# Revit family: Plymold-Essentials-Round_Pedestal-
name_source: partatom
category: Furniture
units: mm (PartAtom-declared; Revit-internal decimal feet)

## family parameters
Always vertical = Yes
Cut with Voids When Loaded = No
OmniClass Number = 23.40.20.00
OmniClass Title = General Furniture and Specialties
Render Appearance Source = Family Geometry
Room Calculation Point = No
Shared = No
Work Plane-Based = No

## types (3) — shared parameters
Assembly Code = E2020200
BASE MATERIAL = PLY - Onyx Black Powdercoat
Brand = Table Bases
Default Elevation = 0"
GLIDES MATERIAL = PLY - Plastic Black
Height = 30"
Keynote = 12500
Manufacturer = Plymold
Product Documentation Link = https://plymold.com
Revit Model Built By = https://www.servex-us.com
Sustainability = https://plymold.com
Type Comments = Tables
URL = https://plymold.com
zero-valued in all types: Cost

## per-type parameters (varying)
| type | Description | Diameter |
| 7162630 | Round Pedestal Dining Height Table Base - 18”Dia x 30”H | 18" |
| 7162730 | Round Pedestal Dining Height Table Base - 22”Dia x 30”H | 22" |
| 7162830 | Round Pedestal Dining Height Table Base - 30”Dia x 30”H | 30" |

note: column(s) folded — value = type name in every type: Model

## geometry (parser evidence)
native form markers: Sweep x8
no freeform markers — native parametric forms only
